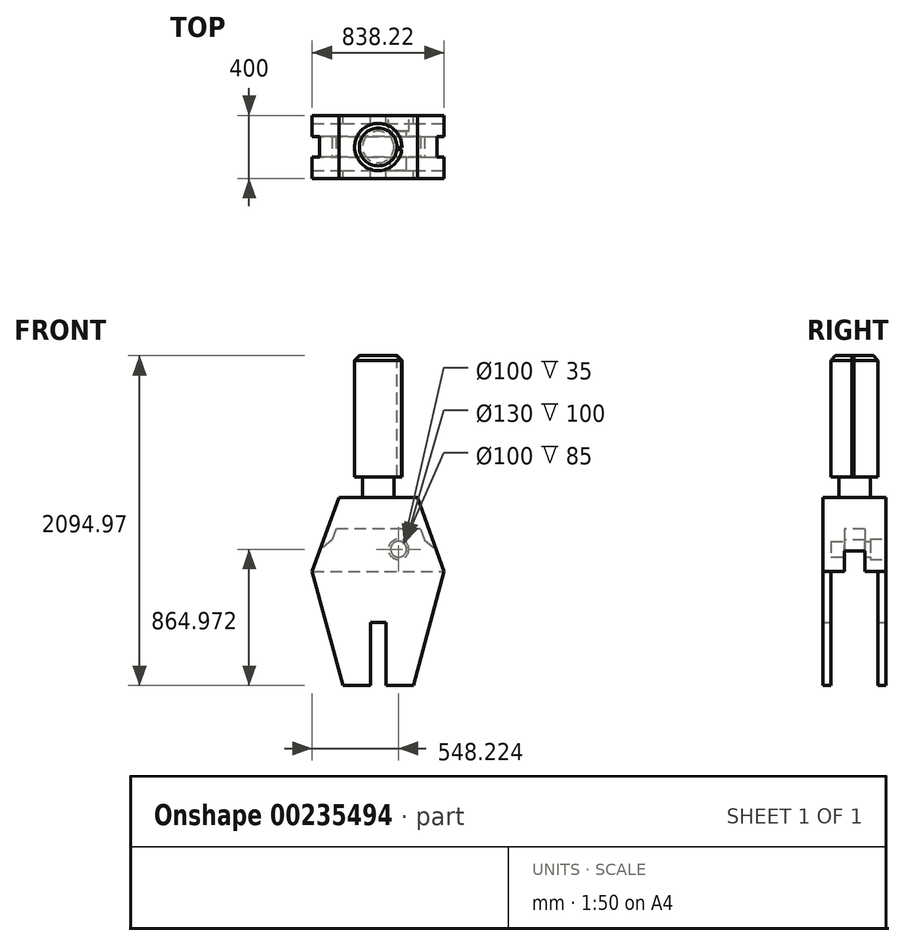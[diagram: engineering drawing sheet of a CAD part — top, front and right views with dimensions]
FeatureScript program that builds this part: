
annotation { "Feature Type Name" : "Feature", "Feature Type Description" : "" }
export const myFeature = defineFeature(function(context is Context, id is Id, definition is map)
    precondition{}
    {
        {
            var Q0;
            Q0=qCreatedBy(makeId("Front.planeOp"),FACE);
            var sketch = newSketch(context, id + "F0", { "sketchPlane" : qUnion([Q0])});
            skLineSegment(sketch, "E0", {"start": v(0, 180.4) * mm, "end": v(-50, 180.4) * mm});
            skLineSegment(sketch, "E1", {"start": v(-50, 180.4) * mm, "end": v(-50, -219.6) * mm});
            skLineSegment(sketch, "E2", {"start": v(-50, -219.6) * mm, "end": v(-225, -219.6) * mm});
            skLineSegment(sketch, "E3", {"start": v(-225, -219.6) * mm, "end": v(-419.11, 504.85) * mm});
            skLineSegment(sketch, "E4", {"start": v(-419.11, 504.85) * mm, "end": v(-250, 975.38) * mm});
            skLineSegment(sketch, "E5", {"start": v(-250, 975.38) * mm, "end": v(0, 975.38) * mm});
            skLineSegment(sketch, "E6", {"start": v(0, 975.38) * mm, "end": v(0, 180.4) * mm});
            skSolve(sketch);
        }
        {
            var Q0;
            Q0=makeQuery(id+"F0.imprint","IMPRINT",FACE,{"disambiguationData":[TD([[makeQuery(id+"F0.imprint","IMPRINT",EDGE,{"derivedFrom":sQuery(id+"F0.wireOp",EDGE,"E0")}),-1.0]])]});
            extrude(context, id + "F1", {"entities" : qUnion([Q0]), "endBound" : BoundingType.SYMMETRIC, "depth" : 400 * mm});
        }
        {
            var Q0;
            Q0=makeQuery(id+"F1.opExtrude","SWEPT_BODY",BODY,{"disambiguationData":[OSD([sQuery(id+"F0.wireOp",EDGE,"E0"),sQuery(id+"F0.wireOp",EDGE,"E1"),sQuery(id+"F0.wireOp",EDGE,"E2"),sQuery(id+"F0.wireOp",EDGE,"E3"),sQuery(id+"F0.wireOp",EDGE,"E4"),sQuery(id+"F0.wireOp",EDGE,"E5"),sQuery(id+"F0.wireOp",EDGE,"E6")])]});
            var Q1;
            Q1=qCreatedBy(makeId("Right.planeOp"),FACE);
            mirror(context, id + "F2", {"operationType" : NewBodyOperationType.ADD, "entities" : qUnion([Q0]), "mirrorPlane" : qUnion([Q1])});
        }
        {
            var Q0;
            Q0=qCreatedBy(makeId("Right.planeOp"),FACE);
            var sketch = newSketch(context, id + "F3", { "sketchPlane" : qUnion([Q0])});
            skLineSegment(sketch, "E7.0", {"start": v(-150, -219.6) * mm, "end": v(150, -219.6) * mm});
            skLineSegment(sketch, "E8.0", {"start": v(-150, 504.85) * mm, "end": v(-65, 504.85) * mm});
            skLineSegment(sketch, "E9", {"start": v(-150, -219.6) * mm, "end": v(-150, 504.85) * mm});
            skLineSegment(sketch, "E10", {"start": v(150, -219.6) * mm, "end": v(150, 504.85) * mm});
            skLineSegment(sketch, "E11", {"start": v(-65, 504.85) * mm, "end": v(-65, 634.85) * mm});
            skLineSegment(sketch, "E12", {"start": v(-65, 634.85) * mm, "end": v(65, 634.85) * mm});
            skLineSegment(sketch, "E13", {"start": v(65, 634.85) * mm, "end": v(65, 504.85) * mm});
            skPoint(sketch, "E14.0.start.orphan", {"position": v(200, -219.6) * mm});
            skPoint(sketch, "E15.0.start.orphan", {"position": v(-200, -219.6) * mm});
            skPoint(sketch, "E16.0.start.orphan", {"position": v(200, 504.85) * mm});
            skPoint(sketch, "E17.0.start.orphan", {"position": v(-200, 504.85) * mm});
            skPoint(sketch, "E18.0.end.orphan", {"position": v(200, 975.38) * mm});
            skPoint(sketch, "E18.0.start.orphan", {"position": v(-200, 975.38) * mm});
            skLineSegment(sketch, "E19.trimOffspring", {"start": v(65, 504.85) * mm, "end": v(150, 504.85) * mm});
            skSolve(sketch);
        }
        {
            var Q0;
            Q0 = qSketchRegion(id + "F3", true);
            extrude(context, id + "F4", {"entities" : qUnion([Q0]), "operationType" : NewBodyOperationType.REMOVE, "endBound" : BoundingType.SYMMETRIC, "oppositeDirection" : true, "depth" : 1000 * mm});
        }
        {
            var Q0;
            Q0=qCreatedBy(makeId("Front.planeOp"),FACE);
            var sketch = newSketch(context, id + "F5", { "sketchPlane" : qUnion([Q0])});
            skLineSegment(sketch, "E20.0", {"start": v(-100, 975.38) * mm, "end": v(0, 975.38) * mm});
            skLineSegment(sketch, "E21", {"start": v(0, 975.38) * mm, "end": v(0, 1875.38) * mm});
            skLineSegment(sketch, "E22", {"start": v(0, 1875.38) * mm, "end": v(-150, 1875.38) * mm});
            skLineSegment(sketch, "E23", {"start": v(-150, 1875.38) * mm, "end": v(-150, 1105.38) * mm});
            skLineSegment(sketch, "E24", {"start": v(-150, 1105.38) * mm, "end": v(-100, 1105.38) * mm});
            skLineSegment(sketch, "E25", {"start": v(-100, 1105.38) * mm, "end": v(-100, 975.38) * mm});
            skPoint(sketch, "E26.orphan", {"position": v(-250, 975.38) * mm});
            skSolve(sketch);
        }
        {
            var Q0;
            Q0=makeQuery(id+"F5.imprint","IMPRINT",FACE,{"disambiguationData":[TD([[makeQuery(id+"F5.imprint","IMPRINT",EDGE,{"derivedFrom":sQuery(id+"F5.wireOp",EDGE,"E20.0")}),1.0]])]});
            var Q1;
            Q1=sQuery(id+"F5.wireOp",EDGE,"E21");
            revolve(context, id + "F6", {"operationType" : NewBodyOperationType.ADD, "entities" : qUnion([Q0]), "axis" : qUnion([Q1]), "revolveType" : RevolveType.FULL});
        }
        {
            var Q0;
            {var subQ0=makeQuery(id+"F1.opExtrude","CAP_FACE",FACE,{"disambiguationData":[OSD([sQuery(id+"F0.wireOp",EDGE,"E0"),sQuery(id+"F0.wireOp",EDGE,"E1"),sQuery(id+"F0.wireOp",EDGE,"E2"),sQuery(id+"F0.wireOp",EDGE,"E3"),sQuery(id+"F0.wireOp",EDGE,"E4"),sQuery(id+"F0.wireOp",EDGE,"E5"),sQuery(id+"F0.wireOp",EDGE,"E6")])],"isStart":true});Q0=makeQuery(id+"F2.boolean.opBoolean","MERGE",FACE,{"derivedFrom":[subQ0,makeQuery(id+"F2.opPattern","COPY",FACE,{"derivedFrom":subQ0,"instanceName":"1"})]});}
            var sketch = newSketch(context, id + "F7", { "sketchPlane" : qUnion([Q0])});
            skCircle(sketch, "E27", {"center": v(-129.11, 645.38) * mm, "radius": 65 * mm});
            skCircle(sketch, "E28", {"center": v(-129.11, 645.38) * mm, "radius": 50 * mm});
            skSolve(sketch);
        }
        {
            var Q0;
            Q0=makeQuery(id+"F7.imprint","IMPRINT",FACE,{"disambiguationData":[TD([[makeQuery(id+"F7.imprint","IMPRINT",EDGE,{"derivedFrom":sQuery(id+"F7.wireOp",EDGE,"E27")}),1.0]])]});
            extrude(context, id + "F8", {"entities" : qUnion([Q0]), "operationType" : NewBodyOperationType.REMOVE, "oppositeDirection" : true, "depth" : 100 * mm});
        }
        {
            var Q0;
            {var subQ0=makeQuery(id+"F1.opExtrude","CAP_FACE",FACE,{"disambiguationData":[OSD([sQuery(id+"F0.wireOp",EDGE,"E0"),sQuery(id+"F0.wireOp",EDGE,"E1"),sQuery(id+"F0.wireOp",EDGE,"E2"),sQuery(id+"F0.wireOp",EDGE,"E3"),sQuery(id+"F0.wireOp",EDGE,"E4"),sQuery(id+"F0.wireOp",EDGE,"E5"),sQuery(id+"F0.wireOp",EDGE,"E6")])],"isStart":true});Q0=makeQuery(id+"F8.boolean.opBoolean","SPLIT",FACE,{"disambiguationData":[TD([makeQuery(id+"F8.opExtrude","SWEPT_FACE",FACE,{"disambiguationData":[OSD([sQuery(id+"F7.wireOp",EDGE,"E28")])]})])],"derivedFrom":makeQuery(id+"F2.boolean.opBoolean","MERGE",FACE,{"derivedFrom":[subQ0,makeQuery(id+"F2.opPattern","COPY",FACE,{"derivedFrom":subQ0,"instanceName":"1"})]})});}
            extrude(context, id + "F9", {"entities" : qUnion([Q0]), "operationType" : NewBodyOperationType.REMOVE, "oppositeDirection" : true, "depth" : 350 * mm});
        }
        {
            var Q0;
            Q0=qCreatedBy(makeId("Front.planeOp"),FACE);
            var sketch = newSketch(context, id + "F10", { "sketchPlane" : qUnion([Q0])});
            skLineSegment(sketch, "E29.0", {"start": v(419.11, 504.85) * mm, "end": v(368.6, 645.38) * mm});
            skLineSegment(sketch, "E30.0", {"start": v(-419.11, 504.85) * mm, "end": v(-368.6, 645.38) * mm});
            skLineSegment(sketch, "E31", {"start": v(419.11, 504.85) * mm, "end": v(-419.11, 504.85) * mm});
            skLineSegment(sketch, "E32", {"start": v(268.75, 775.38) * mm, "end": v(-268.75, 775.38) * mm});
            skLineSegment(sketch, "E33", {"start": v(268.75, 775.38) * mm, "end": v(293.9, 705.38) * mm});
            skLineSegment(sketch, "E34", {"start": v(-268.75, 775.38) * mm, "end": v(-293.9, 705.38) * mm});
            skLineSegment(sketch, "E35", {"start": v(481, 645.38) * mm, "end": v(-606.98, 645.38) * mm, "construction": true});
            skPoint(sketch, "E36", {"position": v(372.4, 634.85) * mm});
            skPoint(sketch, "E37", {"position": v(-372.4, 634.85) * mm});
            skLineSegment(sketch, "E38", {"start": v(293.9, 705.38) * mm, "end": v(372.4, 634.85) * mm});
            skLineSegment(sketch, "E39", {"start": v(-293.9, 705.38) * mm, "end": v(-372.4, 634.85) * mm});
            skPoint(sketch, "E40.orphan", {"position": v(250, 975.38) * mm});
            skPoint(sketch, "E41.orphan", {"position": v(-250, 975.38) * mm});
            skPoint(sketch, "E42.0.0.center.orphan", {"position": v(129.11, 645.38) * mm});
            skPoint(sketch, "E43.0.center.orphan", {"position": v(-129.11, 645.38) * mm});
            skSolve(sketch);
        }
        {
            var Q0;
            Q0 = qSketchRegion(id + "F10", true);
            extrude(context, id + "F11", {"entities" : qUnion([Q0]), "operationType" : NewBodyOperationType.REMOVE, "endBound" : BoundingType.SYMMETRIC, "oppositeDirection" : true, "depth" : 130 * mm});
        }
        {
            var Q0;
            Q0=makeQuery(id+"F6.opRevolve","SWEPT_EDGE",EDGE,{"disambiguationData":[OSD([sQuery(id+"F5.wireOp",EDGE,"E22"),sQuery(id+"F5.wireOp",EDGE,"E23")])]});
            chamfer(context, id + "F12", {"entities" : qUnion([Q0]), "width" : 30 * mm, "tangentPropagation" : true});
        }
        {
            var Q0;
            Q0=makeQuery(id+"F6.opRevolve","SWEPT_FACE",FACE,{"disambiguationData":[OSD([sQuery(id+"F5.wireOp",EDGE,"E22")])]});
            var sketch = newSketch(context, id + "F13", { "sketchPlane" : qUnion([Q0])});
            skLineSegment(sketch, "E44.bottom", {"start": v(120, -5.09) * mm, "end": v(162.04, -5.09) * mm});
            skLineSegment(sketch, "E44.top", {"start": v(120, -15.09) * mm, "end": v(162.04, -15.09) * mm});
            skLineSegment(sketch, "E44.left", {"start": v(120, -5.09) * mm, "end": v(120, -15.09) * mm});
            skLineSegment(sketch, "E44.right", {"start": v(162.04, -5.09) * mm, "end": v(162.04, -15.09) * mm});
            skSolve(sketch);
        }
        {
            var Q0;
            Q0=makeQuery(id+"F13.imprint","IMPRINT",FACE,{"disambiguationData":[TD([[makeQuery(id+"F13.imprint","IMPRINT",EDGE,{"derivedFrom":sQuery(id+"F13.wireOp",EDGE,"E44.bottom")}),-1.0]])]});
            extrude(context, id + "F14", {"entities" : qUnion([Q0]), "operationType" : NewBodyOperationType.REMOVE, "oppositeDirection" : true, "depth" : 770 * mm});
        }
    });
